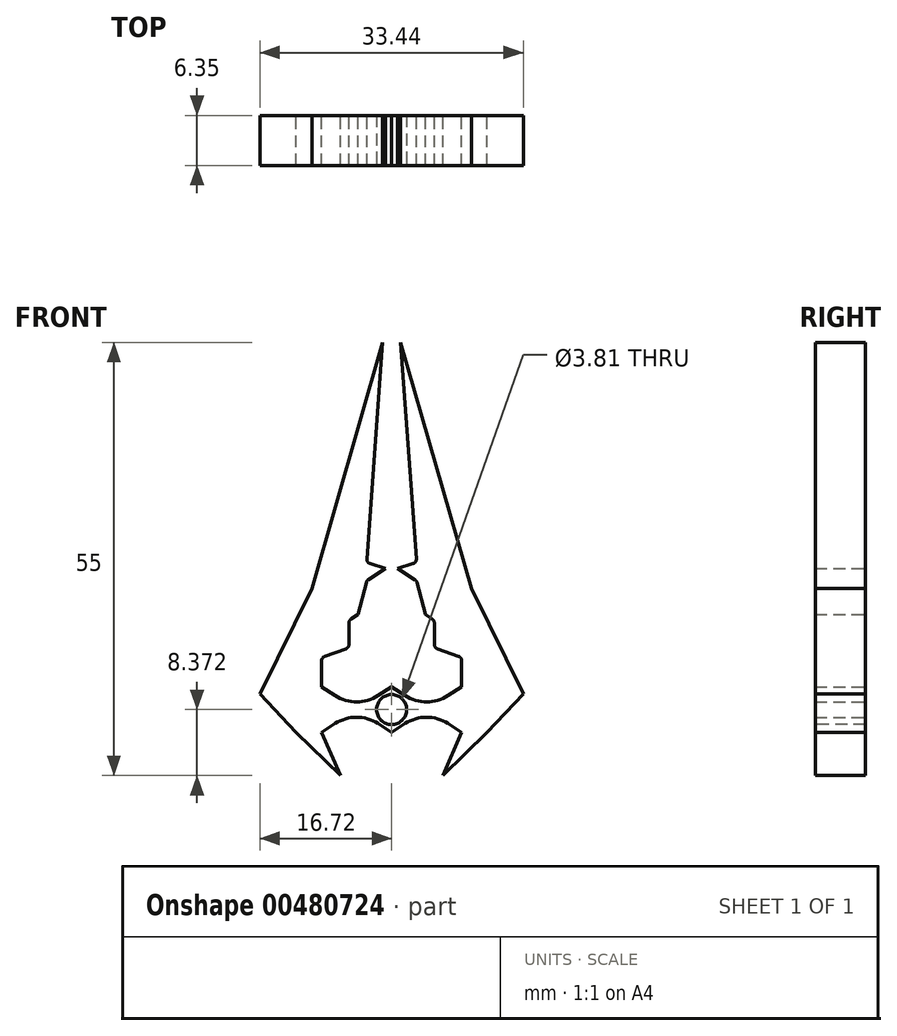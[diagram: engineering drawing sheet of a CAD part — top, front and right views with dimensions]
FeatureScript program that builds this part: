
annotation { "Feature Type Name" : "Feature", "Feature Type Description" : "" }
export const myFeature = defineFeature(function(context is Context, id is Id, definition is map)
    precondition{}
    {
        {
            var Q0;
            Q0=qCreatedBy(makeId("Front.planeOp"),FACE);
            var sketch = newSketch(context, id + "F0", { "sketchPlane" : qUnion([Q0])});
            skLineSegment(sketch, "E0", {"start": v(0, 0) * mm, "end": v(0, 25.4) * mm, "construction": true});
            skLineSegment(sketch, "E1", {"start": v(0, -25.4) * mm, "end": v(0, 0) * mm, "construction": true});
            skLineSegment(sketch, "E2", {"start": v(0, -22.5) * mm, "end": v(8.9, -22.5) * mm, "construction": true});
            skLineSegment(sketch, "E3.MirrorCS", {"start": v(0, -22.5) * mm, "end": v(-8.9, -22.5) * mm, "construction": true});
            skLineSegment(sketch, "E4", {"start": v(0, -25.4) * mm, "end": v(-1.71, -24.28) * mm});
            skLineSegment(sketch, "E5", {"start": v(-7.18, -24.28) * mm, "end": v(-8.89, -25.4) * mm});
            skLineSegment(sketch, "E6", {"start": v(-8.89, -25.4) * mm, "end": v(-8.9, -22.5) * mm});
            skLineSegment(sketch, "E7.MirrorCS", {"start": v(0, -25.4) * mm, "end": v(1.71, -24.28) * mm});
            skLineSegment(sketch, "E8.MirrorCS", {"start": v(7.18, -24.28) * mm, "end": v(8.89, -25.4) * mm});
            skLineSegment(sketch, "E9.MirrorCS", {"start": v(8.89, -25.4) * mm, "end": v(8.9, -22.5) * mm});
            skLineSegment(sketch, "E10.MirrorCS", {"start": v(-8.89, -19.6) * mm, "end": v(-8.9, -22.5) * mm});
            skLineSegment(sketch, "E11.MirrorCS", {"start": v(-7.18, -20.71) * mm, "end": v(-8.89, -19.6) * mm});
            skLineSegment(sketch, "E12.MirrorCS", {"start": v(0, -19.6) * mm, "end": v(-1.71, -20.71) * mm});
            skLineSegment(sketch, "E13.MirrorCS", {"start": v(0, -19.6) * mm, "end": v(1.71, -20.71) * mm});
            skLineSegment(sketch, "E14.MirrorCS", {"start": v(7.18, -20.71) * mm, "end": v(8.89, -19.6) * mm});
            skLineSegment(sketch, "E15.MirrorCS", {"start": v(8.89, -19.6) * mm, "end": v(8.9, -22.5) * mm});
            skPoint(sketch, "E16.visualSharp", {"position": v(4.45, -22.5) * mm});
            skArc(sketch, "E16.filletArc", {"start": v(1.71, -20.71) * mm, "mid": v(4.45, -21.53) * mm, "end": v(7.18, -20.71) * mm});
            skArc(sketch, "E17.filletArc", {"start": v(7.18, -24.28) * mm, "mid": v(4.45, -23.47) * mm, "end": v(1.71, -24.28) * mm});
            skPoint(sketch, "E18.visualSharp", {"position": v(-4.45, -22.5) * mm});
            skArc(sketch, "E18.filletArc", {"start": v(-1.71, -24.28) * mm, "mid": v(-4.45, -23.47) * mm, "end": v(-7.18, -24.28) * mm});
            skArc(sketch, "E19.filletArc", {"start": v(-7.18, -20.71) * mm, "mid": v(-4.45, -21.53) * mm, "end": v(-1.71, -20.71) * mm});
            skLineSegment(sketch, "E20", {"start": v(-8.89, -25.4) * mm, "end": v(-6.5, -30.87) * mm});
            skLineSegment(sketch, "E21", {"start": v(-6.5, -30.87) * mm, "end": v(-12.13, -25.4) * mm});
            skLineSegment(sketch, "E22", {"start": v(-12.13, -25.4) * mm, "end": v(-16.72, -20.5) * mm});
            skLineSegment(sketch, "E23", {"start": v(-1.13, 24.13) * mm, "end": v(-3.13, -3.37) * mm});
            skLineSegment(sketch, "E24", {"start": v(-2.73, -3.96) * mm, "end": v(-0.76, -4.57) * mm});
            skLineSegment(sketch, "E25", {"start": v(-0.76, -4.57) * mm, "end": v(-2.98, -6) * mm});
            skLineSegment(sketch, "E26.MirrorCS", {"start": v(1.13, 24.13) * mm, "end": v(3.13, -3.37) * mm});
            skLineSegment(sketch, "E27.MirrorCS", {"start": v(2.73, -3.96) * mm, "end": v(0.76, -4.57) * mm});
            skLineSegment(sketch, "E28.MirrorCS", {"start": v(0.76, -4.57) * mm, "end": v(2.98, -6) * mm});
            skLineSegment(sketch, "E29.MirrorCS", {"start": v(12.13, -25.4) * mm, "end": v(16.72, -20.5) * mm});
            skLineSegment(sketch, "E30.MirrorCS", {"start": v(6.5, -30.87) * mm, "end": v(12.13, -25.4) * mm});
            skLineSegment(sketch, "E31.MirrorCS", {"start": v(8.89, -25.4) * mm, "end": v(6.5, -30.87) * mm});
            skLineSegment(sketch, "E32", {"start": v(-16.72, -20.5) * mm, "end": v(-10.14, -7.08) * mm});
            skLineSegment(sketch, "E33", {"start": v(-10.14, -7.08) * mm, "end": v(-1.13, 24.13) * mm});
            skLineSegment(sketch, "E34.MirrorCS", {"start": v(10.14, -7.08) * mm, "end": v(1.13, 24.13) * mm});
            skLineSegment(sketch, "E35.MirrorCS", {"start": v(16.72, -20.5) * mm, "end": v(10.14, -7.08) * mm});
            skLineSegment(sketch, "E36", {"start": v(-3.22, -6.35) * mm, "end": v(-4.28, -10.43) * mm});
            skLineSegment(sketch, "E37", {"start": v(-4.28, -10.43) * mm, "end": v(-5.16, -11) * mm});
            skLineSegment(sketch, "E38", {"start": v(-5.42, -11.5) * mm, "end": v(-5.42, -14.22) * mm});
            skLineSegment(sketch, "E39", {"start": v(-5.8, -14.76) * mm, "end": v(-8.5, -15.74) * mm});
            skLineSegment(sketch, "E40", {"start": v(-8.89, -16.29) * mm, "end": v(-8.89, -19.6) * mm});
            skLineSegment(sketch, "E41.MirrorCS", {"start": v(3.22, -6.35) * mm, "end": v(4.28, -10.43) * mm});
            skLineSegment(sketch, "E42.MirrorCS", {"start": v(4.28, -10.43) * mm, "end": v(5.16, -11) * mm});
            skLineSegment(sketch, "E43.MirrorCS", {"start": v(5.42, -11.5) * mm, "end": v(5.42, -14.22) * mm});
            skLineSegment(sketch, "E44.MirrorCS", {"start": v(5.8, -14.76) * mm, "end": v(8.5, -15.74) * mm});
            skLineSegment(sketch, "E45.MirrorCS", {"start": v(8.89, -16.29) * mm, "end": v(8.89, -19.6) * mm});
            skPoint(sketch, "E46.visualSharp", {"position": v(-3.17, -3.83) * mm});
            skArc(sketch, "E46.filletArc", {"start": v(-3.13, -3.37) * mm, "mid": v(-3.03, -3.74) * mm, "end": v(-2.73, -3.96) * mm});
            skPoint(sketch, "E47.visualSharp", {"position": v(3.17, -3.83) * mm});
            skArc(sketch, "E47.filletArc", {"start": v(2.73, -3.96) * mm, "mid": v(3.03, -3.74) * mm, "end": v(3.13, -3.37) * mm});
            skPoint(sketch, "E48.visualSharp", {"position": v(-5.42, -11.18) * mm});
            skArc(sketch, "E48.filletArc", {"start": v(-5.16, -11) * mm, "mid": v(-5.35, -11.21) * mm, "end": v(-5.42, -11.5) * mm});
            skPoint(sketch, "E49.visualSharp", {"position": v(5.42, -11.18) * mm});
            skArc(sketch, "E49.filletArc", {"start": v(5.42, -11.5) * mm, "mid": v(5.35, -11.21) * mm, "end": v(5.16, -11) * mm});
            skPoint(sketch, "E50.visualSharp", {"position": v(3.17, -6.13) * mm});
            skArc(sketch, "E50.filletArc", {"start": v(3.22, -6.35) * mm, "mid": v(3.13, -6.15) * mm, "end": v(2.98, -6) * mm});
            skPoint(sketch, "E51.visualSharp", {"position": v(-3.17, -6.13) * mm});
            skArc(sketch, "E51.filletArc", {"start": v(-2.98, -6) * mm, "mid": v(-3.13, -6.15) * mm, "end": v(-3.22, -6.35) * mm});
            skPoint(sketch, "E52.visualSharp", {"position": v(-5.42, -14.63) * mm});
            skArc(sketch, "E52.filletArc", {"start": v(-5.8, -14.76) * mm, "mid": v(-5.53, -14.55) * mm, "end": v(-5.42, -14.22) * mm});
            skPoint(sketch, "E53.visualSharp", {"position": v(5.42, -14.63) * mm});
            skArc(sketch, "E53.filletArc", {"start": v(5.42, -14.22) * mm, "mid": v(5.53, -14.55) * mm, "end": v(5.8, -14.76) * mm});
            skPoint(sketch, "E54.visualSharp", {"position": v(-8.89, -15.88) * mm});
            skArc(sketch, "E54.filletArc", {"start": v(-8.5, -15.74) * mm, "mid": v(-8.78, -15.96) * mm, "end": v(-8.9, -16.29) * mm});
            skPoint(sketch, "E55.visualSharp", {"position": v(8.89, -15.88) * mm});
            skArc(sketch, "E55.filletArc", {"start": v(8.89, -16.29) * mm, "mid": v(8.78, -15.96) * mm, "end": v(8.5, -15.74) * mm});
            skSolve(sketch);
        }
        {
            var Q0;
            Q0=makeQuery(id+"F0.imprint","IMPRINT",FACE,{"disambiguationData":[TD([[makeQuery(id+"F0.imprint","IMPRINT",EDGE,{"derivedFrom":sQuery(id+"F0.wireOp",EDGE,"E6")}),1.0]])]});
            var Q1;
            Q1=makeQuery(id+"F0.imprint","IMPRINT",FACE,{"disambiguationData":[TD([[makeQuery(id+"F0.imprint","IMPRINT",EDGE,{"derivedFrom":sQuery(id+"F0.wireOp",EDGE,"E9.MirrorCS")}),-1.0]])]});
            var Q2;
            Q2=makeQuery(id+"F0.imprint","IMPRINT",FACE,{"disambiguationData":[TD([[makeQuery(id+"F0.imprint","IMPRINT",EDGE,{"derivedFrom":sQuery(id+"F0.wireOp",EDGE,"E4")}),-1.0]])]});
            extrude(context, id + "F1", {"entities" : qUnion([Q0, Q1, Q2]), "depth" : 6.35 * mm, "offsetDistance" : 25 * mm});
        }
        {
            var Q0;
            Q0=makeQuery(id+"F1.opExtrude","CAP_FACE",FACE,{"disambiguationData":[OSD([sQuery(id+"F0.wireOp",EDGE,"E4"),sQuery(id+"F0.wireOp",EDGE,"E5"),sQuery(id+"F0.wireOp",EDGE,"E7.MirrorCS"),sQuery(id+"F0.wireOp",EDGE,"E8.MirrorCS"),sQuery(id+"F0.wireOp",EDGE,"E11.MirrorCS"),sQuery(id+"F0.wireOp",EDGE,"E12.MirrorCS"),sQuery(id+"F0.wireOp",EDGE,"E13.MirrorCS"),sQuery(id+"F0.wireOp",EDGE,"E14.MirrorCS"),sQuery(id+"F0.wireOp",EDGE,"E16.filletArc"),sQuery(id+"F0.wireOp",EDGE,"E17.filletArc"),sQuery(id+"F0.wireOp",EDGE,"E18.filletArc"),sQuery(id+"F0.wireOp",EDGE,"E19.filletArc"),sQuery(id+"F0.wireOp",EDGE,"E20"),sQuery(id+"F0.wireOp",EDGE,"E21"),sQuery(id+"F0.wireOp",EDGE,"E22"),sQuery(id+"F0.wireOp",EDGE,"E23"),sQuery(id+"F0.wireOp",EDGE,"E24"),sQuery(id+"F0.wireOp",EDGE,"E25"),sQuery(id+"F0.wireOp",EDGE,"E26.MirrorCS"),sQuery(id+"F0.wireOp",EDGE,"E27.MirrorCS"),sQuery(id+"F0.wireOp",EDGE,"E28.MirrorCS"),sQuery(id+"F0.wireOp",EDGE,"E29.MirrorCS"),sQuery(id+"F0.wireOp",EDGE,"E30.MirrorCS"),sQuery(id+"F0.wireOp",EDGE,"E31.MirrorCS"),sQuery(id+"F0.wireOp",EDGE,"E32"),sQuery(id+"F0.wireOp",EDGE,"E33"),sQuery(id+"F0.wireOp",EDGE,"E34.MirrorCS"),sQuery(id+"F0.wireOp",EDGE,"E35.MirrorCS"),sQuery(id+"F0.wireOp",EDGE,"E36"),sQuery(id+"F0.wireOp",EDGE,"E37"),sQuery(id+"F0.wireOp",EDGE,"E38"),sQuery(id+"F0.wireOp",EDGE,"E39"),sQuery(id+"F0.wireOp",EDGE,"E40"),sQuery(id+"F0.wireOp",EDGE,"E41.MirrorCS"),sQuery(id+"F0.wireOp",EDGE,"E42.MirrorCS"),sQuery(id+"F0.wireOp",EDGE,"E43.MirrorCS"),sQuery(id+"F0.wireOp",EDGE,"E44.MirrorCS"),sQuery(id+"F0.wireOp",EDGE,"E45.MirrorCS"),sQuery(id+"F0.wireOp",EDGE,"E46.filletArc"),sQuery(id+"F0.wireOp",EDGE,"E47.filletArc"),sQuery(id+"F0.wireOp",EDGE,"E48.filletArc"),sQuery(id+"F0.wireOp",EDGE,"E49.filletArc"),sQuery(id+"F0.wireOp",EDGE,"E50.filletArc"),sQuery(id+"F0.wireOp",EDGE,"E51.filletArc"),sQuery(id+"F0.wireOp",EDGE,"E52.filletArc"),sQuery(id+"F0.wireOp",EDGE,"E53.filletArc"),sQuery(id+"F0.wireOp",EDGE,"E54.filletArc"),sQuery(id+"F0.wireOp",EDGE,"E55.filletArc")])],"isStart":false});
            var sketch = newSketch(context, id + "F2", { "sketchPlane" : qUnion([Q0])});
            skLineSegment(sketch, "E56", {"start": v(0, -19.6) * mm, "end": v(0, -25.4) * mm, "construction": true});
            skCircle(sketch, "E57", {"center": v(0, -22.5) * mm, "radius": 1.9 * mm});
            skSolve(sketch);
        }
        {
            var Q0;
            Q0=makeQuery(id+"F2.imprint","IMPRINT",FACE,{"disambiguationData":[TD([[makeQuery(id+"F2.imprint","IMPRINT",EDGE,{"derivedFrom":sQuery(id+"F2.wireOp",EDGE,"E57")}),1.0]])]});
            extrude(context, id + "F3", {"entities" : qUnion([Q0]), "operationType" : NewBodyOperationType.REMOVE, "oppositeDirection" : true, "depth" : 25 * mm, "offsetDistance" : 25 * mm});
        }
    });
